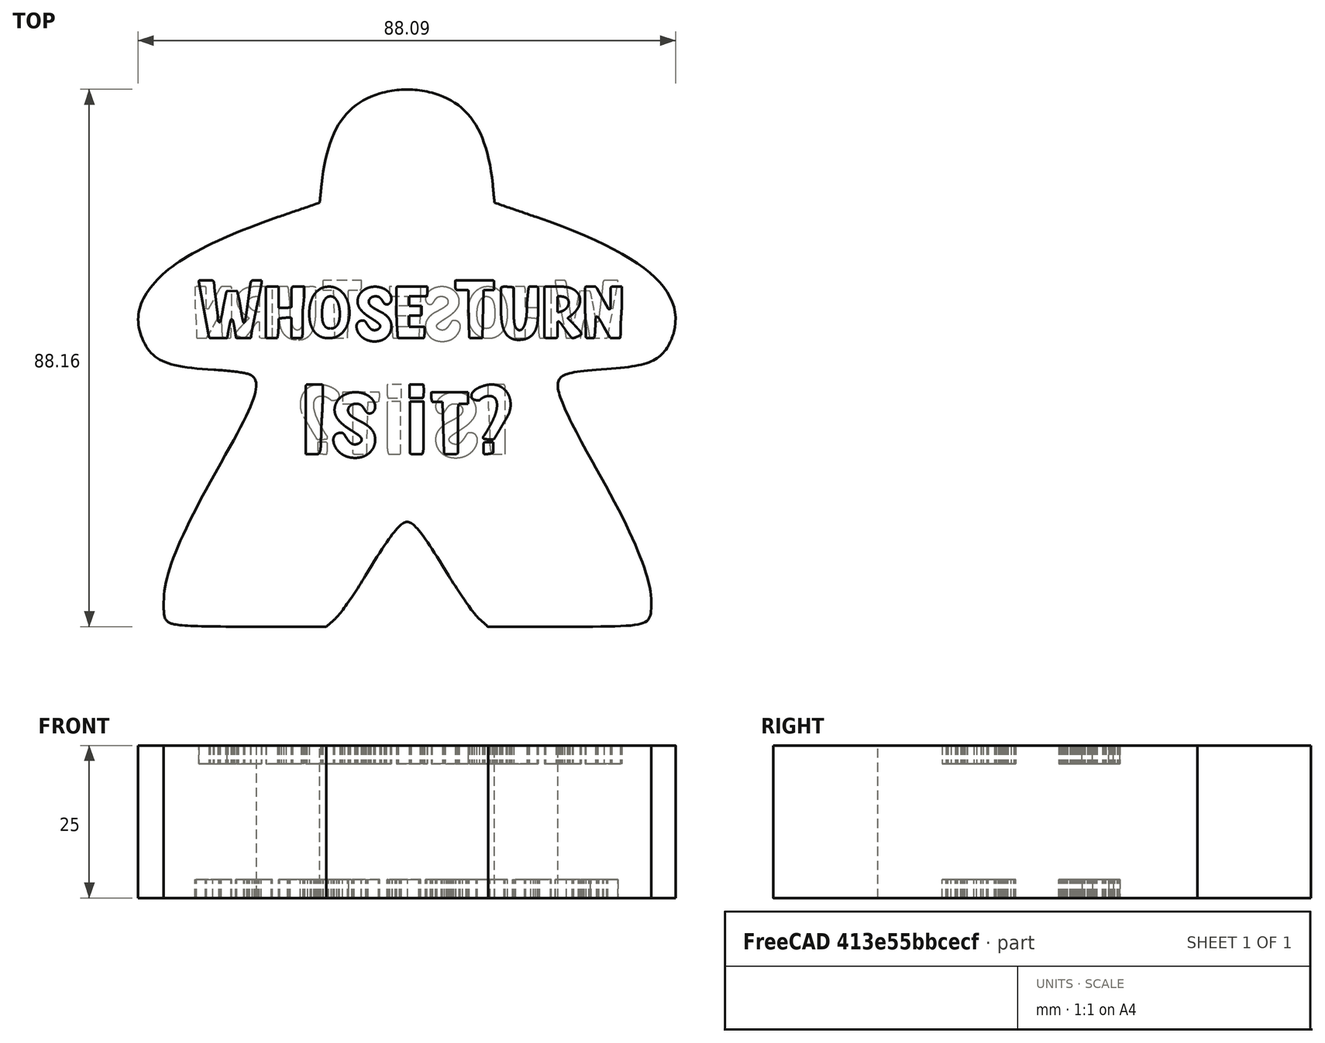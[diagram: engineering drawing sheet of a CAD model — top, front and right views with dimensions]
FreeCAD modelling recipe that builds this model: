
FCSTD DOCUMENT  (FreeCAD 0.20R29410 (Git))
Label: WhoseTurnIsItMeeple02
License: All rights reserved
LicenseURL: http://en.wikipedia.org/wiki/All_rights_reserved
objects: Part::Part2DObjectPython×4, PartDesign::Pocket×4, PartDesign::Plane×2, Sketcher::SketchObject×1, PartDesign::Pad×1, PartDesign::Body×1
note: 18 computed .brp shape members not serialized (recipe doc carries the construction recipe); baked Part::Feature solids carry a one-line shape summary decoded from their .brp

FEATURE [Sketcher::SketchObject] Sketch001  label="Meeple"
  FullyConstrained = false
  sketch-geometry (32):
    g0: BSplineCurve PolesCount=4 KnotsCount=2 Degree=3 IsPeriodic=0
    g1: BSplineCurve PolesCount=4 KnotsCount=2 Degree=3 IsPeriodic=0
    g2: BSplineCurve PolesCount=4 KnotsCount=2 Degree=3 IsPeriodic=0
    g3: BSplineCurve PolesCount=4 KnotsCount=2 Degree=3 IsPeriodic=0
    g4: BSplineCurve PolesCount=4 KnotsCount=2 Degree=3 IsPeriodic=0
    g5: BSplineCurve PolesCount=4 KnotsCount=2 Degree=3 IsPeriodic=0
    g6: BSplineCurve PolesCount=4 KnotsCount=2 Degree=3 IsPeriodic=0
    g7: BSplineCurve PolesCount=2 KnotsCount=2 Degree=1 IsPeriodic=0
    g8: BSplineCurve PolesCount=2 KnotsCount=2 Degree=1 IsPeriodic=0
    g9: BSplineCurve PolesCount=4 KnotsCount=2 Degree=3 IsPeriodic=0
    g10: BSplineCurve PolesCount=4 KnotsCount=2 Degree=3 IsPeriodic=0
    g11: BSplineCurve PolesCount=4 KnotsCount=2 Degree=3 IsPeriodic=0
    g12: BSplineCurve PolesCount=2 KnotsCount=2 Degree=1 IsPeriodic=0
    g13: BSplineCurve PolesCount=2 KnotsCount=2 Degree=1 IsPeriodic=0
    g14: BSplineCurve PolesCount=4 KnotsCount=2 Degree=3 IsPeriodic=0
    g15: BSplineCurve PolesCount=4 KnotsCount=2 Degree=3 IsPeriodic=0
    g16: BSplineCurve PolesCount=4 KnotsCount=2 Degree=3 IsPeriodic=0
    g17: BSplineCurve PolesCount=4 KnotsCount=2 Degree=3 IsPeriodic=0
    g18: BSplineCurve PolesCount=4 KnotsCount=2 Degree=3 IsPeriodic=0
    g19: BSplineCurve PolesCount=4 KnotsCount=2 Degree=3 IsPeriodic=0
    g20: BSplineCurve PolesCount=4 KnotsCount=2 Degree=3 IsPeriodic=0
    g21: BSplineCurve PolesCount=2 KnotsCount=2 Degree=1 IsPeriodic=0
    g22: BSplineCurve PolesCount=2 KnotsCount=2 Degree=1 IsPeriodic=0
    g23: BSplineCurve PolesCount=4 KnotsCount=2 Degree=3 IsPeriodic=0
    g24: BSplineCurve PolesCount=4 KnotsCount=2 Degree=3 IsPeriodic=0
    g25: BSplineCurve PolesCount=4 KnotsCount=2 Degree=3 IsPeriodic=0
    g26: BSplineCurve PolesCount=4 KnotsCount=2 Degree=3 IsPeriodic=0
    g27: BSplineCurve PolesCount=2 KnotsCount=2 Degree=1 IsPeriodic=0
    g28: BSplineCurve PolesCount=2 KnotsCount=2 Degree=1 IsPeriodic=0
    g29: BSplineCurve PolesCount=4 KnotsCount=2 Degree=3 IsPeriodic=0
    g30: LineSegment StartX=-4.5 StartY=-42 StartZ=0 EndX=95.5 EndY=-42 EndZ=0
    g31: LineSegment StartX=-4.5 StartY=-60 StartZ=0 EndX=95.5 EndY=-59.7727 EndZ=0
  constraints (37):
    c: Coincident(g0,g1)
    c: Coincident(g1,g2)
    c: Coincident(g2,g3)
    c: Coincident(g3,g4)
    c: Coincident(g4,g5)
    c: Coincident(g5,g6)
    c: Coincident(g6,g7)
    c: Coincident(g7,g8)
    c: Coincident(g8,g9)
    c: Coincident(g9,g10)
    c: Coincident(g10,g11)
    c: Coincident(g11,g12)
    c: Coincident(g12,g13)
    c: Coincident(g13,g14)
    c: Coincident(g14,g15)
    c: Coincident(g15,g16)
    c: Coincident(g16,g17)
    c: Coincident(g17,g18)
    c: Coincident(g18,g19)
    c: Coincident(g19,g20)
    c: Coincident(g20,g21)
    c: Coincident(g21,g22)
    c: Coincident(g22,g23)
    c: Coincident(g23,g24)
    c: Coincident(g24,g25)
    c: Coincident(g25,g26)
    c: Coincident(g26,g27)
    c: Coincident(g27,g28)
    c: Coincident(g28,g29)
    c: Coincident(g29,g0)
    c: DistanceX(g30,g30) = 100
    c: Horizontal(g30)
    c: DistanceX(g30) = -4.5
    c: DistanceY(g30) = -42
    c: DistanceX(g31,g31) = 100
    c: Vertical(g31,g30)
    c: DistanceY(g31,g30) = 18
FEATURE [PartDesign::Pad] Pad
  Direction = (0,0,1)
  Length = 25
  Length2 = 10
  Profile = -> Sketch001
  ReferenceAxis = -> Sketch001 [N_Axis]
  Refine = true
  Type = 0
FEATURE [PartDesign::Plane] DatumPlane
  Length = 135.951
  MapMode = 5
  Placement = pos=(0,0,25) rot=(0,0,1;0rad)
  ResizeMode = 0
  Support = -> [Pad]
  Width = 135.995
FEATURE [PartDesign::Plane] DatumPlane001
  AttachmentOffset = pos=(0,0,0) rot=(0,0,1;3.14159rad)
  Length = 135.951
  MapMode = 5
  Placement = pos=(0,0,0) rot=(0,-1,0;3.14159rad)
  ResizeMode = 0
  Support = -> [Pad]
  Width = 135.995
FEATURE [Part::Part2DObjectPython] ShapeString  label="Whose  Turn Top"  # Draft 2D object (typed FeaturePython)
  AttachmentOffset = pos=(10,-41,0) rot=(0,0,1;0rad)
  FontFile = <userpath>/Downloads/fonts/every-run-font/EveryRunRegular-ZV5pK.ttf
  MakeFace = true
  MapMode = 5
  Placement = pos=(10,-41,25) rot=(0,0,1;0rad)
  Size = 5
  String = Whose Turn
  Support = -> [DatumPlane]
  Tracking = 0
FEATURE [Part::Part2DObjectPython] ShapeString001  label="Is It? Top"  # Draft 2D object (typed FeaturePython)
  AttachmentOffset = pos=(27,-60,0) rot=(0,0,1;0rad)
  FontFile = <userpath>/Downloads/fonts/every-run-font/EveryRunRegular-ZV5pK.ttf
  MakeFace = true
  MapMode = 5
  Placement = pos=(27,-60,25) rot=(0,0,1;0rad)
  Size = 6
  String = Is it?
  Support = -> [DatumPlane]
  Tracking = 0
FEATURE [PartDesign::Pocket] Pocket
  BaseFeature = -> Pad
  Direction = (0,0,-1)
  Length = 3
  Length2 = 5
  Profile = -> ShapeString
  ReferenceAxis = -> ShapeString [N_Axis]
  Refine = true
  Type = 0
FEATURE [PartDesign::Pocket] Pocket001
  BaseFeature = -> Pocket
  Direction = (0,0,-1)
  Length = 3
  Length2 = 5
  Profile = -> ShapeString001
  ReferenceAxis = -> ShapeString001 [N_Axis]
  Refine = true
  Type = 0
FEATURE [Part::Part2DObjectPython] ShapeString002  label="Whose  Turn Top001"  # Draft 2D object (typed FeaturePython)
  AttachmentOffset = pos=(-79,-41,0) rot=(0,0,1;0rad)
  FontFile = <userpath>/Downloads/fonts/every-run-font/EveryRunRegular-ZV5pK.ttf
  MakeFace = true
  MapMode = 5
  Placement = pos=(79,-41,0) rot=(0,1,0;3.14159rad)
  Size = 5
  String = Whose Turn
  Support = -> [DatumPlane001]
  Tracking = 0
FEATURE [Part::Part2DObjectPython] ShapeString003  label="Is It? Top001"  # Draft 2D object (typed FeaturePython)
  AttachmentOffset = pos=(-61,-60,0) rot=(0,0,1;0rad)
  FontFile = <userpath>/Downloads/fonts/every-run-font/EveryRunRegular-ZV5pK.ttf
  MakeFace = true
  MapMode = 5
  Placement = pos=(61,-60,0) rot=(0,1,0;3.14159rad)
  Size = 6
  String = Is it?
  Support = -> [DatumPlane001]
  Tracking = 0
FEATURE [PartDesign::Pocket] Pocket002
  BaseFeature = -> Pocket001
  Direction = (0,0,1)
  Length = 3
  Length2 = 5
  Profile = -> ShapeString002
  ReferenceAxis = -> ShapeString002 [N_Axis]
  Refine = true
  Type = 0
FEATURE [PartDesign::Pocket] Pocket003
  BaseFeature = -> Pocket002
  Direction = (0,0,1)
  Length = 3
  Length2 = 5
  Profile = -> ShapeString003
  ReferenceAxis = -> ShapeString003 [N_Axis]
  Refine = true
  Type = 0
FEATURE [PartDesign::Body] Body
  Group = -> [Sketch001,Pad,DatumPlane,DatumPlane001,ShapeString,ShapeString001,Pocket,Pocket001,ShapeString002,ShapeString003,Pocket002,Pocket003]
  Origin = -> Origin
  Tip = -> Pocket003
